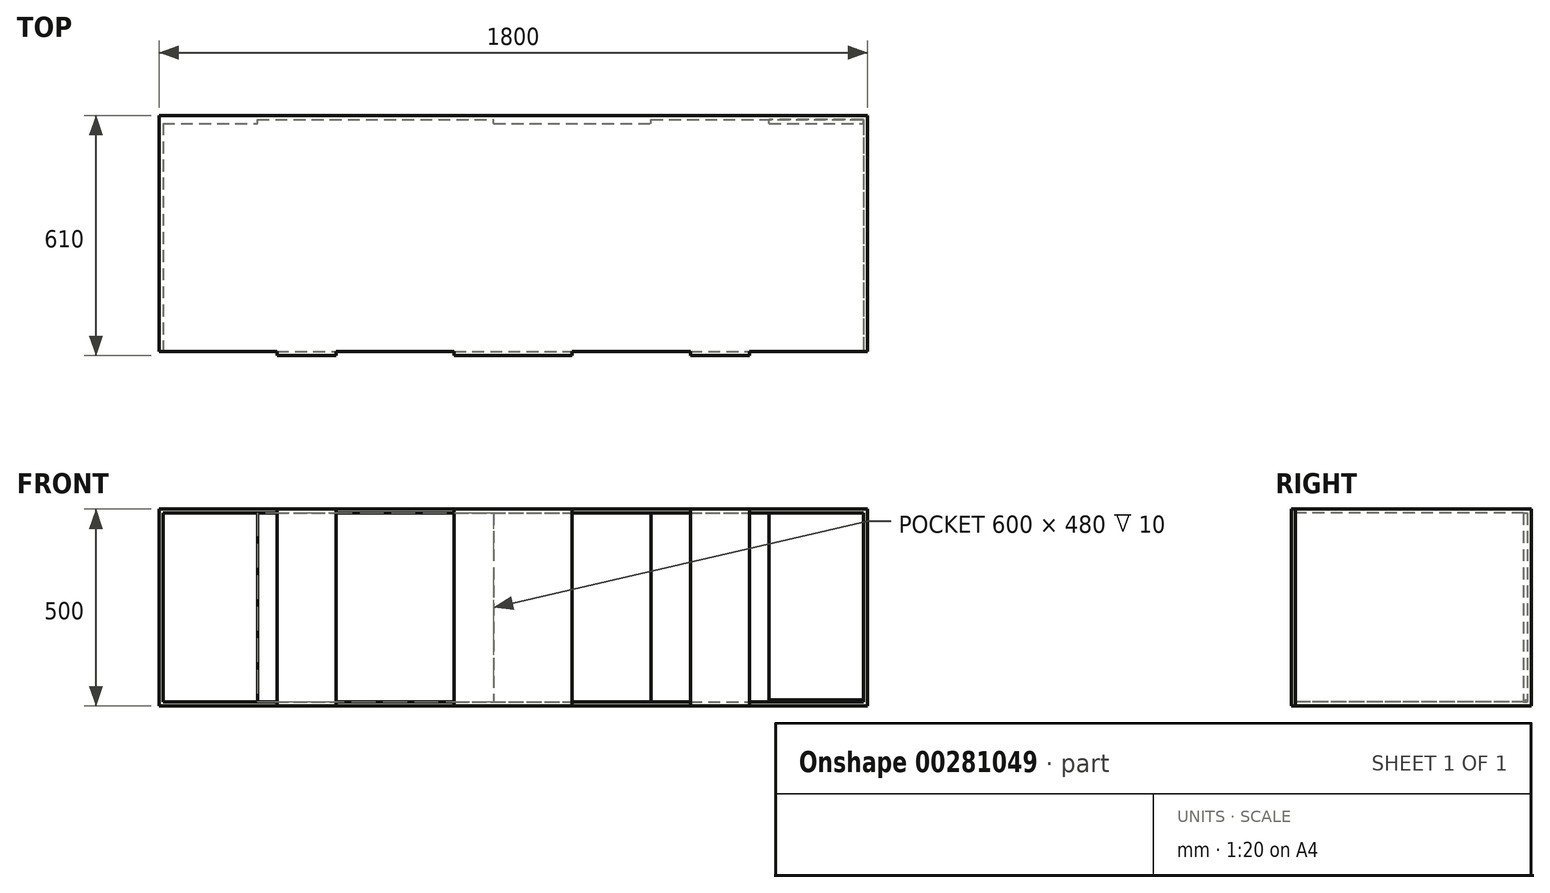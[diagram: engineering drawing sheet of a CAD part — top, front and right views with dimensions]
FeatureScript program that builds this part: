
annotation { "Feature Type Name" : "Feature", "Feature Type Description" : "" }
export const myFeature = defineFeature(function(context is Context, id is Id, definition is map)
    precondition{}
    {
        {
            var Q0;
            Q0=qCreatedBy(makeId("Front.planeOp"),FACE);
            var sketch = newSketch(context, id + "F0", { "sketchPlane" : qUnion([Q0])});
            skLineSegment(sketch, "E0.bottom", {"start": v(900, -250) * mm, "end": v(-900, -250) * mm});
            skLineSegment(sketch, "E0.top", {"start": v(900, 250) * mm, "end": v(-900, 250) * mm});
            skLineSegment(sketch, "E0.left", {"start": v(900, -250) * mm, "end": v(900, 250) * mm});
            skLineSegment(sketch, "E0.right", {"start": v(-900, -250) * mm, "end": v(-900, 250) * mm});
            skPoint(sketch, "E0.middle", {"position": v(0, 0) * mm});
            skSolve(sketch);
        }
        {
            var Q0;
            Q0 = qSketchRegion(id + "F0", true);
            extrude(context, id + "F1", {"entities" : qUnion([Q0]), "depth" : 600 * mm});
        }
        {
            var Q0;
            Q0=makeQuery(id+"F1.opExtrude","CAP_FACE",FACE,{"disambiguationData":[OSD([sQuery(id+"F0.wireOp",EDGE,"E0.bottom"),sQuery(id+"F0.wireOp",EDGE,"E0.top"),sQuery(id+"F0.wireOp",EDGE,"E0.left"),sQuery(id+"F0.wireOp",EDGE,"E0.right")])],"isStart":false});
            var sketch = newSketch(context, id + "F2", { "sketchPlane" : qUnion([Q0])});
            skLineSegment(sketch, "E1.bottom", {"start": v(-890, 240) * mm, "end": v(890, 240) * mm});
            skLineSegment(sketch, "E1.top", {"start": v(-890, -240) * mm, "end": v(890, -240) * mm});
            skLineSegment(sketch, "E1.left", {"start": v(-890, 240) * mm, "end": v(-890, -240) * mm});
            skLineSegment(sketch, "E1.right", {"start": v(890, 240) * mm, "end": v(890, -240) * mm});
            skPoint(sketch, "E1.middle", {"position": v(0, 0) * mm});
            skSolve(sketch);
        }
        {
            var Q0;
            Q0 = qSketchRegion(id + "F2", true);
            extrude(context, id + "F3", {"entities" : qUnion([Q0]), "operationType" : NewBodyOperationType.REMOVE, "oppositeDirection" : true, "depth" : 590 * mm});
        }
        {
            var Q0;
            Q0=makeQuery(id+"F1.opExtrude","SWEPT_FACE",FACE,{"disambiguationData":[OSD([sQuery(id+"F0.wireOp",EDGE,"E0.bottom")])]});
            var sketch = newSketch(context, id + "F4", { "sketchPlane" : qUnion([Q0])});
            skSolve(sketch);
        }
        {
            var Q0;
            {var subQ0=sQuery(id+"F0.wireOp",EDGE,"E0.bottom");Q0=makeQuery(id+"F4.imprint","IMPRINT",FACE,{"disambiguationData":[TD([[makeQuery(id+"F4.imprint","IMPRINT",EDGE,{"derivedFrom":makeQuery(id+"F1.opExtrude","CAP_EDGE",EDGE,{"disambiguationData":[OSD([subQ0])],"isStart":true})}),-1.0]])]});}
            var sketch = newSketch(context, id + "F5", { "sketchPlane" : qUnion([Q0])});
            skLineSegment(sketch, "E2.bottom", {"start": v(-600, 610) * mm, "end": v(-450, 610) * mm});
            skLineSegment(sketch, "E2.top", {"start": v(-600, 600) * mm, "end": v(-450, 600) * mm});
            skLineSegment(sketch, "E2.left", {"start": v(-450, 610) * mm, "end": v(-450, 600) * mm});
            skLineSegment(sketch, "E2.right", {"start": v(-600, 610) * mm, "end": v(-600, 600) * mm});
            skLineSegment(sketch, "E3.bottom", {"start": v(-150, 600) * mm, "end": v(150, 600) * mm});
            skLineSegment(sketch, "E3.top", {"start": v(-150, 610) * mm, "end": v(150, 610) * mm});
            skLineSegment(sketch, "E3.left", {"start": v(-150, 600) * mm, "end": v(-150, 610) * mm});
            skLineSegment(sketch, "E3.right", {"start": v(150, 600) * mm, "end": v(150, 610) * mm});
            skLineSegment(sketch, "E4.bottom", {"start": v(1421.64, 912.1) * mm, "end": v(2108.02, 912.1) * mm});
            skLineSegment(sketch, "E4.top", {"start": v(1421.64, 922.1) * mm, "end": v(2108.02, 922.1) * mm});
            skLineSegment(sketch, "E4.left", {"start": v(1421.64, 912.1) * mm, "end": v(1421.64, 922.1) * mm});
            skLineSegment(sketch, "E4.right", {"start": v(2108.02, 912.1) * mm, "end": v(2108.02, 922.1) * mm});
            skLineSegment(sketch, "E5.bottom", {"start": v(450, 600) * mm, "end": v(600, 600) * mm});
            skLineSegment(sketch, "E5.top", {"start": v(450, 610) * mm, "end": v(600, 610) * mm});
            skLineSegment(sketch, "E5.left", {"start": v(450, 600) * mm, "end": v(450, 610) * mm});
            skLineSegment(sketch, "E5.right", {"start": v(600, 600) * mm, "end": v(600, 610) * mm});
            skSolve(sketch);
        }
        {
            var Q0;
            Q0=makeQuery(id+"F5.imprint","IMPRINT",FACE,{"disambiguationData":[TD([[makeQuery(id+"F5.imprint","IMPRINT",EDGE,{"derivedFrom":sQuery(id+"F5.wireOp",EDGE,"E5.bottom")}),-1.0]])]});
            var Q1;
            Q1=makeQuery(id+"F5.imprint","IMPRINT",FACE,{"disambiguationData":[TD([[makeQuery(id+"F5.imprint","IMPRINT",EDGE,{"derivedFrom":sQuery(id+"F5.wireOp",EDGE,"E3.bottom")}),-1.0]])]});
            var Q2;
            Q2=makeQuery(id+"F5.imprint","IMPRINT",FACE,{"disambiguationData":[TD([[makeQuery(id+"F5.imprint","IMPRINT",EDGE,{"derivedFrom":sQuery(id+"F5.wireOp",EDGE,"E2.bottom")}),-1.0]])]});
            extrude(context, id + "F7", {"entities" : qUnion([Q0, Q1, Q2]), "operationType" : NewBodyOperationType.ADD, "oppositeDirection" : true, "depth" : 500 * mm});
        }
        {
            var Q0;
            Q0=makeQuery(id+"F3.boolean.opBoolean","COPY",FACE,{"derivedFrom":makeQuery(id+"F3.opExtrude","CAP_FACE",FACE,{"disambiguationData":[OSD([sQuery(id+"F2.wireOp",EDGE,"E1.bottom"),sQuery(id+"F2.wireOp",EDGE,"E1.top"),sQuery(id+"F2.wireOp",EDGE,"E1.left"),sQuery(id+"F2.wireOp",EDGE,"E1.right")])],"isStart":false})});
            var sketch = newSketch(context, id + "F6", { "sketchPlane" : qUnion([Q0])});
            skLineSegment(sketch, "E6.bottom", {"start": v(-890, 240) * mm, "end": v(-650, 240) * mm});
            skLineSegment(sketch, "E6.top", {"start": v(-890, -240) * mm, "end": v(-650, -240) * mm});
            skLineSegment(sketch, "E6.left", {"start": v(-890, 240) * mm, "end": v(-890, -240) * mm});
            skLineSegment(sketch, "E6.right", {"start": v(-650, 240) * mm, "end": v(-650, -240) * mm});
            skLineSegment(sketch, "E7.bottom", {"start": v(-50, 240) * mm, "end": v(350, 240) * mm});
            skLineSegment(sketch, "E7.top", {"start": v(-50, -240) * mm, "end": v(350, -240) * mm});
            skLineSegment(sketch, "E7.left", {"start": v(-50, 240) * mm, "end": v(-50, -240) * mm});
            skLineSegment(sketch, "E7.right", {"start": v(350, 240) * mm, "end": v(350, -240) * mm});
            skLineSegment(sketch, "E8.bottom", {"start": v(890, 240) * mm, "end": v(650, 240) * mm});
            skLineSegment(sketch, "E8.top", {"start": v(890, -234.8) * mm, "end": v(650, -234.8) * mm});
            skLineSegment(sketch, "E8.left", {"start": v(890, 240) * mm, "end": v(890, -234.8) * mm});
            skLineSegment(sketch, "E8.right", {"start": v(650, 240) * mm, "end": v(650, -234.8) * mm});
            skSolve(sketch);
        }
        {
            var Q0;
            Q0 = qSketchRegion(id + "F6", true);
            extrude(context, id + "F8", {"entities" : qUnion([Q0]), "operationType" : NewBodyOperationType.ADD, "depth" : 10 * mm});
        }
    });
